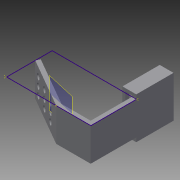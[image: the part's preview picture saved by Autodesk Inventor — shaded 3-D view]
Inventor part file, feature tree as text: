
AUTODESK INVENTOR PART (.ipt)
format: ipt  version: 2015 (Build 190159000, 159)  size: 206,336 bytes
history: native  units: mm
features: sketch x14, extrude x13, pattern_linear x2, plane x1
ambient origin geometry x8: Origin, YZ Plane, XZ Plane, XY Plane, X Axis, Y Axis, Z Axis, Center Point
bodies: Solid1 (feature_tree)
feature tree (30):
  extrude  "Extrusion1"  Depth=24.0mm
  extrude  "Extrusion2"  Depth=3.0mm
  pattern_linear  "Rectangular Pattern1"  Count1=3 Spacing1=12.0mm
  extrude  "Extrusion3"  Depth=25.0mm TaperAngle=0.0deg
  extrude  "Extrusion4"  Depth=57.0mm TaperAngle=0.0deg
  extrude  "Extrusion5"  Depth=3.0mm
  extrude  "Extrusion6"  Depth=2.0mm
  extrude  "Extrusion7"  Depth=2.0mm
  extrude  "Extrusion8"  Depth=24.0mm TaperAngle=0.0deg
  sketch  "Sketch9"  dims[d23=2.0mm d24=2.0mm]
  extrude  "Extrusion10"  Depth=3.0mm TaperAngle=0.0deg
  extrude  "Extrusion11"  Depth=1.0mm
  sketch  "Sketch12"  dims[d34=1.0mm d35=1.0mm]
  plane  "Work Plane1"
  extrude  "Extrusion14"  Depth=24.0mm TaperAngle=0.0deg
  extrude  "Extrusion15"  Depth=3.0mm
  extrude  "Extrusion16"  Depth=24.0mm TaperAngle=0.0deg
  pattern_linear  "Rectangular Pattern2"  Spacing1=24.0mm  [1 undecoded]
  sketch  "Sketch1"  dims[d0=36.0mm d1=24.0mm]
  sketch  "Sketch2"  dims[d2=3.0mm d3=0.0mm d4=4.25mm]
  sketch  "Sketch3"  dims[d5=4.25mm]
  sketch  "Sketch4"  dims[d6=0.0mm d7=30.0mm d9=12.0mm]
  sketch  "Sketch5"  dims[d10=30.0mm d12=6.0mm d13=25.0mm d14=0.0mm]
  sketch  "Sketch6"  dims[d15=3.0mm d16=57.0mm d17=0.0mm]
  sketch  "Sketch7"  dims[d18=24.0mm d19=3.0mm]
  sketch  "Sketch8"  dims[d20=7.0mm d21=0.0mm d22=2.0mm]
  sketch  "Sketch10"  dims[d25=2.0mm d26=24.0mm d27=0.0mm]
  sketch  "Sketch11"  dims[d28=3.0mm d29=0.0mm d30=3.0mm d31=0.0mm]
  sketch  "Sketch15"  dims[d36=10.0mm d37=0.0mm d38=24.0mm d39=0.0mm]
  sketch  "Sketch16"  dims[d47=30.0deg d48=3.0mm d49=24.0mm d50=0.0mm d51=24.0mm d52=0.0mm d53=6.0mm d54=4.25mm d55=24.0mm d56=0.0mm d57=30.0mm d59=12.0mm d60=30.0mm d62=6.0mm]
note: 1 required parameter value undecoded (feature->parameter linkage not recoverable at this tier; creation-order binding heuristic only, values carry confidence <= 0.55)
